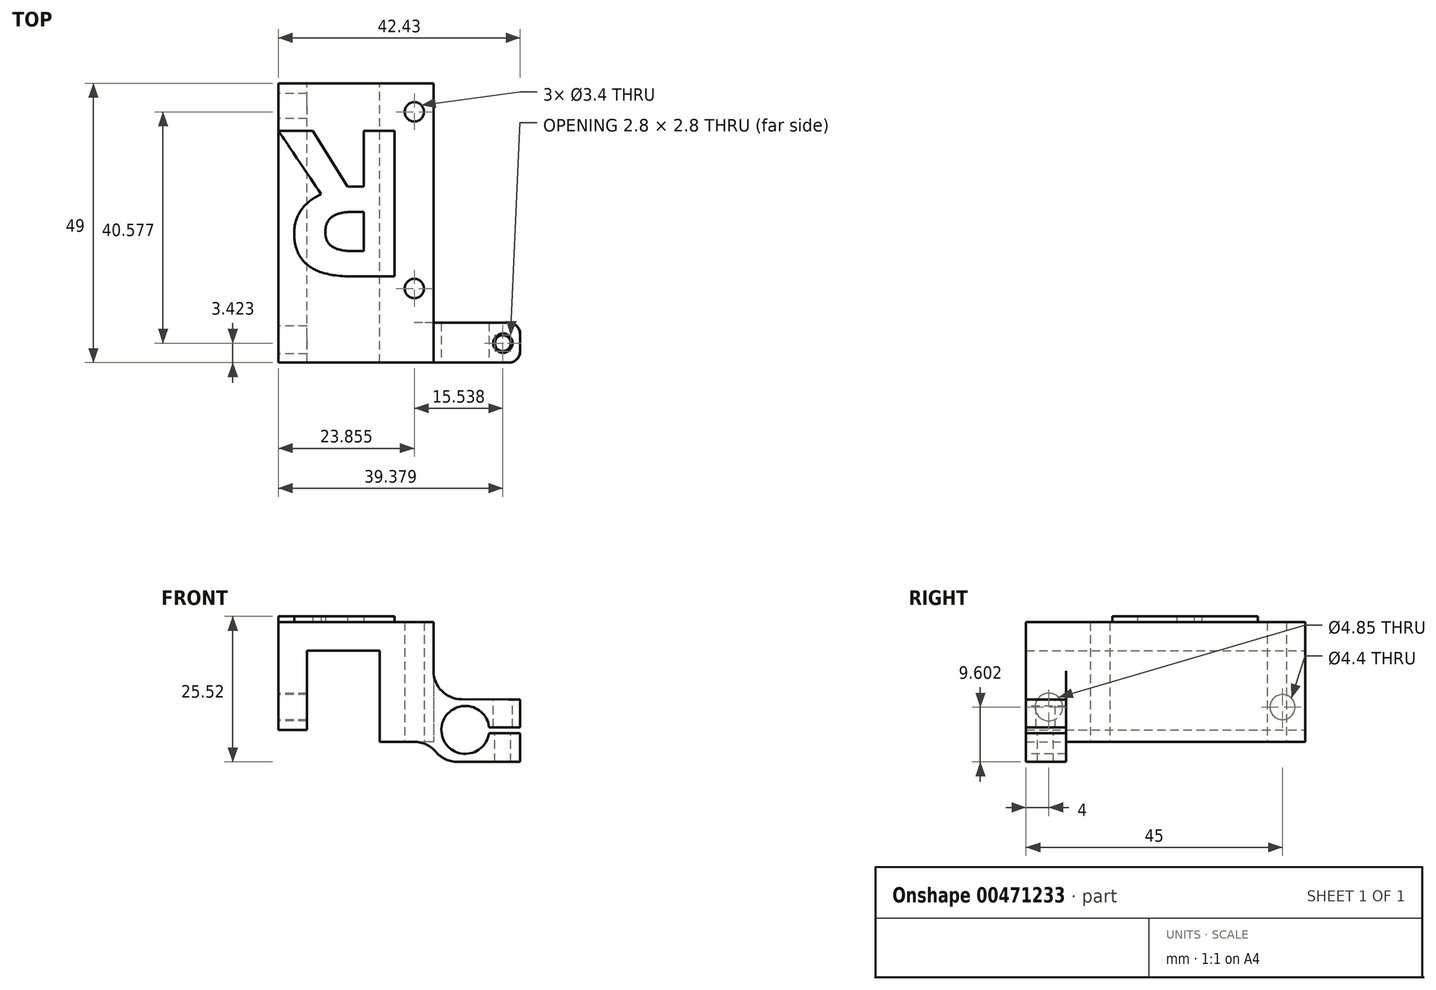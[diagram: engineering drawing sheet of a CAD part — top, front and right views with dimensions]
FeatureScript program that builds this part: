
annotation { "Feature Type Name" : "Feature", "Feature Type Description" : "" }
export const myFeature = defineFeature(function(context is Context, id is Id, definition is map)
    precondition{}
    {
        {
            var Q0;
            Q0=qCreatedBy(makeId("Front.planeOp"),FACE);
            var sketch = newSketch(context, id + "F0", { "sketchPlane" : qUnion([Q0])});
            skLineSegment(sketch, "E0", {"start": v(-18.67, 10.9) * mm, "end": v(-18.67, 29.8) * mm});
            skLineSegment(sketch, "E1", {"start": v(-18.67, 29.8) * mm, "end": v(8.54, 29.8) * mm});
            skLineSegment(sketch, "E2", {"start": v(8.54, 29.8) * mm, "end": v(8.54, 16.27) * mm});
            skLineSegment(sketch, "E3", {"start": v(-0.87, 8.8) * mm, "end": v(-0.87, 24.8) * mm});
            skLineSegment(sketch, "E4", {"start": v(-0.87, 24.8) * mm, "end": v(-13.67, 24.8) * mm});
            skLineSegment(sketch, "E5", {"start": v(-13.67, 24.8) * mm, "end": v(-13.67, 10.9) * mm});
            skLineSegment(sketch, "E6", {"start": v(-13.67, 10.9) * mm, "end": v(-18.67, 10.9) * mm});
            skLineSegment(sketch, "E7", {"start": v(8.54, 16.27) * mm, "end": v(8.54, 8.8) * mm});
            skLineSegment(sketch, "E8", {"start": v(8.54, 8.8) * mm, "end": v(-0.87, 8.8) * mm});
            skLineSegment(sketch, "E9", {"start": v(8.54, 16.27) * mm, "end": v(8.54, 16.27) * mm});
            skLineSegment(sketch, "E10", {"start": v(23.73, 16.24) * mm, "end": v(23.73, 11.34) * mm});
            skLineSegment(sketch, "E11", {"start": v(23.73, 11.34) * mm, "end": v(17.09, 11.34) * mm});
            skLineSegment(sketch, "E12", {"start": v(17.09, 11.34) * mm, "end": v(17.09, 10.34) * mm});
            skLineSegment(sketch, "E13", {"start": v(17.09, 10.34) * mm, "end": v(23.76, 10.34) * mm});
            skLineSegment(sketch, "E14", {"start": v(23.76, 10.34) * mm, "end": v(23.76, 5.29) * mm});
            skLineSegment(sketch, "E15", {"start": v(23.76, 5.29) * mm, "end": v(9.95, 5.29) * mm});
            skLineSegment(sketch, "E16", {"start": v(9.95, 5.29) * mm, "end": v(8.54, 8.8) * mm});
            skLineSegment(sketch, "E17", {"start": v(23.73, 16.24) * mm, "end": v(8.54, 16.27) * mm});
            skSolve(sketch);
        }
        {
            var Q0;
            Q0=makeQuery(id+"F0.imprint","IMPRINT",FACE,{"disambiguationData":[TD([[makeQuery(id+"F0.imprint","IMPRINT",EDGE,{"derivedFrom":sQuery(id+"F0.wireOp",EDGE,"E0")}),-1.0]])]});
            var Q1;
            {var subQ2=sQuery(id+"F0.wireOp",EDGE,"69cbcc5d-e0c3-48db-8baf-3487a8abab7d");Q1=makeQuery(id+"F0.imprint","IMPRINT",FACE,{"disambiguationData":[TD([[makeQuery(id+"F0.imprint","IMPRINT",EDGE,{"derivedFrom":subQ2}),-1.0]])]});}
            var Q2;
            Q2=makeQuery(id+"F0.imprint","IMPRINT",FACE,{"disambiguationData":[TD([[makeQuery(id+"F0.imprint","IMPRINT",EDGE,{"derivedFrom":sQuery(id+"F0.wireOp",EDGE,"E7")}),1.0]])]});
            extrude(context, id + "F1", {"entities" : qUnion([Q0, Q1, Q2]), "depth" : 7 * mm});
        }
        {
            var Q0;
            Q0=makeQuery(id+"F0.imprint","IMPRINT",FACE,{"disambiguationData":[TD([[makeQuery(id+"F0.imprint","IMPRINT",EDGE,{"derivedFrom":sQuery(id+"F0.wireOp",EDGE,"E0")}),-1.0]])]});
            extrude(context, id + "F2", {"entities" : qUnion([Q0]), "operationType" : NewBodyOperationType.ADD, "oppositeDirection" : true, "depth" : 42 * mm});
        }
        {
            var Q0;
            {var subQ0=sQuery(id+"F0.wireOp",EDGE,"E8");Q0=makeQuery(id+"F2.boolean.opBoolean","MERGE",FACE,{"derivedFrom":[makeQuery(id+"F1.opExtrude","SWEPT_FACE",FACE,{"disambiguationData":[OSD([subQ0])]}),makeQuery(id+"F2.opExtrude","SWEPT_FACE",FACE,{"disambiguationData":[OSD([subQ0])]})]});}
            var sketch = newSketch(context, id + "F3", { "sketchPlane" : qUnion([Q0])});
            skCircle(sketch, "E18", {"center": v(5.19, -6) * mm, "radius": 1.7 * mm});
            skCircle(sketch, "E19", {"center": v(5.19, -37) * mm, "radius": 1.7 * mm});
            skCircle(sketch, "E20", {"center": v(20.69, -21.5) * mm, "radius": 11 * mm});
            skSolve(sketch);
        }
        {
            var Q0;
            Q0=qSketchRegion(id+"F3",true);
            extrude(context, id + "F4", {"entities" : qUnion([Q0]), "operationType" : NewBodyOperationType.REMOVE, "endBound" : BoundingType.THROUGH_ALL, "oppositeDirection" : true, "depth" : 25 * mm});
        }
        {
            var Q0;
            Q0=makeQuery(id+"F1.opExtrude","CAP_FACE",FACE,{"disambiguationData":[OSD([sQuery(id+"F0.wireOp",EDGE,"E0"),sQuery(id+"F0.wireOp",EDGE,"E1"),sQuery(id+"F0.wireOp",EDGE,"E2"),sQuery(id+"F0.wireOp",EDGE,"E3"),sQuery(id+"F0.wireOp",EDGE,"E4"),sQuery(id+"F0.wireOp",EDGE,"E5"),sQuery(id+"F0.wireOp",EDGE,"E6"),sQuery(id+"F0.wireOp",EDGE,"E8"),sQuery(id+"F0.wireOp",EDGE,"E9"),sQuery(id+"F0.wireOp",EDGE,"58f11638-63e7-4b32-8aff-a1ba3c53649b"),sQuery(id+"F0.wireOp",EDGE,"E10"),sQuery(id+"F0.wireOp",EDGE,"E11"),sQuery(id+"F0.wireOp",EDGE,"E12"),sQuery(id+"F0.wireOp",EDGE,"E13"),sQuery(id+"F0.wireOp",EDGE,"E14"),sQuery(id+"F0.wireOp",EDGE,"E15"),sQuery(id+"F0.wireOp",EDGE,"E16")])],"isStart":false});
            var sketch = newSketch(context, id + "F5", { "sketchPlane" : qUnion([Q0])});
            skCircle(sketch, "E21", {"center": v(14.13, 10.9) * mm, "radius": 4.2 * mm});
            skSolve(sketch);
        }
        {
            var Q0;
            Q0=qSketchRegion(id+"F5",true);
            extrude(context, id + "F6", {"entities" : qUnion([Q0]), "operationType" : NewBodyOperationType.REMOVE, "oppositeDirection" : true, "depth" : 10 * mm});
        }
        {
            var Q0;
            Q0=qSketchRegion(id+"F3",true);
            extrude(context, id + "F7", {"entities" : qUnion([Q0]), "operationType" : NewBodyOperationType.REMOVE, "endBound" : BoundingType.THROUGH_ALL, "oppositeDirection" : true, "depth" : 25 * mm});
        }
        {
            var Q0;
            Q0=makeQuery(id+"F1.opExtrude","SWEPT_FACE",FACE,{"disambiguationData":[OSD([sQuery(id+"F0.wireOp",EDGE,"E17")])]});
            var sketch = newSketch(context, id + "F8", { "sketchPlane" : qUnion([Q0])});
            skCircle(sketch, "E22", {"center": v(20.7, -3.58) * mm, "radius": 1.7 * mm});
            skCircle(sketch, "E23", {"center": v(20.7, -3.58) * mm, "radius": 1.4 * mm});
            skSolve(sketch);
        }
        {
            var Q0;
            Q0=makeQuery(id+"F8.imprint","IMPRINT",FACE,{"disambiguationData":[TD([[makeQuery(id+"F8.imprint","IMPRINT",EDGE,{"derivedFrom":sQuery(id+"F8.wireOp",EDGE,"E23")}),1.0]])]});
            extrude(context, id + "F9", {"entities" : qUnion([Q0]), "operationType" : NewBodyOperationType.REMOVE, "endBound" : BoundingType.THROUGH_ALL, "oppositeDirection" : true, "depth" : 25 * mm});
        }
        {
            var Q0;
            Q0=makeQuery(id+"F8.imprint","IMPRINT",FACE,{"disambiguationData":[TD([[makeQuery(id+"F8.imprint","IMPRINT",EDGE,{"derivedFrom":sQuery(id+"F8.wireOp",EDGE,"E22")}),1.0]])]});
            extrude(context, id + "F10", {"entities" : qUnion([Q0]), "operationType" : NewBodyOperationType.REMOVE, "endBound" : BoundingType.UP_TO_NEXT, "oppositeDirection" : true, "depth" : 25 * mm});
        }
        {
            var Q0;
            Q0=makeQuery(id+"F1.opExtrude","SWEPT_EDGE",EDGE,{"disambiguationData":[OSD([sQuery(id+"F0.wireOp",EDGE,"E2"),sQuery(id+"F0.wireOp",EDGE,"E7"),sQuery(id+"F0.wireOp",EDGE,"E17")])]});
            fillet(context, id + "F11", {"entities" : qUnion([Q0]), "radius" : 5 * mm, "tangentPropagation" : true, "allowEdgeOverflow" : false});
        }
        {
            var Q0;
            Q0=makeQuery(id+"F1.opExtrude","SWEPT_EDGE",EDGE,{"disambiguationData":[OSD([sQuery(id+"F0.wireOp",EDGE,"E7"),sQuery(id+"F0.wireOp",EDGE,"E8"),sQuery(id+"F0.wireOp",EDGE,"E16")])]});
            fillet(context, id + "F12", {"entities" : qUnion([Q0]), "radius" : 5 * mm, "tangentPropagation" : true, "allowEdgeOverflow" : false});
        }
        {
            var Q0;
            Q0=makeQuery(id+"F1.opExtrude","SWEPT_EDGE",EDGE,{"disambiguationData":[OSD([sQuery(id+"F0.wireOp",EDGE,"E15"),sQuery(id+"F0.wireOp",EDGE,"E16")])]});
            fillet(context, id + "F13", {"entities" : qUnion([Q0]), "radius" : 5 * mm, "tangentPropagation" : true, "allowEdgeOverflow" : false});
        }
        {
            var Q0;
            Q0=makeQuery(id+"F1.opExtrude","CAP_EDGE",EDGE,{"disambiguationData":[OSD([sQuery(id+"F0.wireOp",EDGE,"E10")])],"isStart":false});
            var Q1;
            Q1=makeQuery(id+"F1.opExtrude","CAP_EDGE",EDGE,{"disambiguationData":[OSD([sQuery(id+"F0.wireOp",EDGE,"E14")])],"isStart":false});
            var Q2;
            Q2=makeQuery(id+"F1.opExtrude","CAP_EDGE",EDGE,{"disambiguationData":[OSD([sQuery(id+"F0.wireOp",EDGE,"E10")])],"isStart":true});
            var Q3;
            Q3=makeQuery(id+"F1.opExtrude","CAP_EDGE",EDGE,{"disambiguationData":[OSD([sQuery(id+"F0.wireOp",EDGE,"E14")])],"isStart":true});
            fillet(context, id + "F14", {"entities" : qUnion([Q0, Q1, Q2, Q3]), "radius" : 2 * mm, "tangentPropagation" : true, "allowEdgeOverflow" : false});
        }
        {
            var Q0;
            {var subQ0=sQuery(id+"F0.wireOp",EDGE,"E0");Q0=makeQuery(id+"F2.boolean.opBoolean","MERGE",FACE,{"derivedFrom":[makeQuery(id+"F1.opExtrude","SWEPT_FACE",FACE,{"disambiguationData":[OSD([subQ0])]}),makeQuery(id+"F2.opExtrude","SWEPT_FACE",FACE,{"disambiguationData":[OSD([subQ0])]})]});}
            var sketch = newSketch(context, id + "F15", { "sketchPlane" : qUnion([Q0])});
            skCircle(sketch, "E24", {"center": v(-38, 14.9) * mm, "radius": 2.2 * mm});
            skCircle(sketch, "E25", {"center": v(3, 14.9) * mm, "radius": 2.43 * mm});
            skSolve(sketch);
        }
        {
            var Q0;
            Q0=qSketchRegion(id+"F15",true);
            extrude(context, id + "F16", {"entities" : qUnion([Q0]), "operationType" : NewBodyOperationType.REMOVE, "oppositeDirection" : true, "depth" : 6 * mm});
        }
        {
            var Q0;
            {var subQ0=sQuery(id+"F0.wireOp",EDGE,"E1");Q0=makeQuery(id+"F2.boolean.opBoolean","MERGE",FACE,{"derivedFrom":[makeQuery(id+"F1.opExtrude","SWEPT_FACE",FACE,{"disambiguationData":[OSD([subQ0])]}),makeQuery(id+"F2.opExtrude","SWEPT_FACE",FACE,{"disambiguationData":[OSD([subQ0])]})]});}
            var sketch = newSketch(context, id + "F17", { "sketchPlane" : qUnion([Q0])});
            skText(sketch, "E26", { "text": "R", "fontName": "OpenSans-Bold.ttf"});
            const initialGuessF17  = {"E26": [0.00494, 0.03366, -1, 0, 0.02575]};
            skSetInitialGuess(sketch, initialGuessF17);
            skSolve(sketch);
        }
        {
            var Q0;
            Q0=qSketchRegion(id+"F17",true);
            extrude(context, id + "F18", {"entities" : qUnion([Q0]), "operationType" : NewBodyOperationType.ADD, "depth" : 1 * mm});
        }
        {
            var Q0;
            Q0 = qSketchRegion(id + "F3", true);
            extrude(context, id + "F19", {"entities" : qUnion([Q0]), "operationType" : NewBodyOperationType.REMOVE, "endBound" : BoundingType.THROUGH_ALL, "oppositeDirection" : true, "depth" : 25 * mm});
        }
    });
